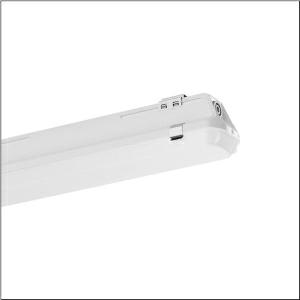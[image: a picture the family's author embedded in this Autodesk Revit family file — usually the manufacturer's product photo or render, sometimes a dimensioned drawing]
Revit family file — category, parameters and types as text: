
# Revit family: monsun_r__21_51fb12mp480b_d2d7
name_source: partatom
category: Lighting Fixtures
units: mm (PartAtom-declared; Revit-internal decimal feet)

## family parameters
Cut with Voids When Loaded = No
Host = Face
Light Source = No
Part Type = Normal
Room Calculation Point = No
Round Connector Dimension = Use Diameter
Shared = No

## types (1)
- --- (1 x LED, 8100 lm, 53.6 W, 4000K)
    Apparent Load = 54 VA
    CIE Flux Codes = 65 88 97 97 100
    Color Rendering = 80
    Color Temperature = 4000K
    Default Elevation = 1800 mm
    Description = Monsun® 21, damp-proof luminaire, chain hanger, primary light control with lens, primary optical cover: enclosure, of PMMA, light emission: direct distribution, primary light characteristic: symmetric, installation type: suspended mounting, surface-mounted, horizontal mounting, vertical mounting, LED, rated luminous flux: 8.100lm, luminous efficacy: 151lm/W, light colour: 840, colour temperature: 4000K, control gear: ECG, with terminal, 3-pole, max. 2.5mm², mains connection: 220..240V, AC, 50/60Hz, rated input power: 54W, housing, of glass-fibre reinforced polyester, uncoated, bright grey, incl. chain hanger, length: 1.590mm, width: 90mm, height: 88mm, clip for enclosure, of stainless steel (V2A), ceiling mounting element, of stainless steel (V2A), chain hanger, of stainless steel (V2A), protection rating (complete): IP66, insulation class (complete): insulation class I (protective earthing), certification: CE, ENEC, VDE, UKCA, protection symbol: D, impact resistance: IK04, permissible operating ambient temperature: -25..+35°C, standard: EN 50419, EN 60598-2-1, corresponds to IFS (International Featured Standards) requirements for safety and quality in the food industry, for indoor or canopied outdoor use, no direct snow, no direct sun, no direct rain, contact your sales advisor before using the luminaires in applications with unclear chemical exposure, large temperature fluctuations or condensation-forming humidity, LABS conformity tested according to VDMA 24364:2018-05, packaging unit: 1 piece
    Height = 89 mm
    Lamp = 1 x LED
    Lamp Light Flux = 8100 lm
    Lamp Power = 53.6 W
    Lamp count = 1
    Length = 1590 mm
    Luminous efficacy = 151 lm/W
    Manufacturer = Siteco
    ModVariant = No
    Model = 51FB12MP480B
    Mounting Place = Ceiling
    Mounting Type = Surface mounted
    Number of Poles = 1
    OnlyDefault = Yes
    Power Factor = 1
    Product Name = Monsun® 21
    Product group = damp-proof luminaire
    ProductGroupID = 300
    Protection Class = Protection class I
    Protection Degree = IP 66
    RLX_Detail_Level = 1
    RLX_Emergency_Light_Flux = 0 lm
    RLX_Emergency_Type = 0
    RLX_Emergency_Type_DB = No
    RlxData = <blob elided: 90257 chars, md5=f6598f29>
    Socket = socket
    Standby Power = 0 W
    System Light Flux = 8100 lm
    System Power = 54 W
    Type Comments = factory setting: luminous flux: 100 % | (A | C | E) | 121 mA
    Type Image = l_1319656.jpg
    URL = http://relux.com
    VarID = @adj_117111
    Voltage = 0 V
    Weight = 0.00 kg
    Width = 90 mm

## geometry (parser evidence)
native form markers: Blend x4, Sweep x9
no freeform markers — native parametric forms only
